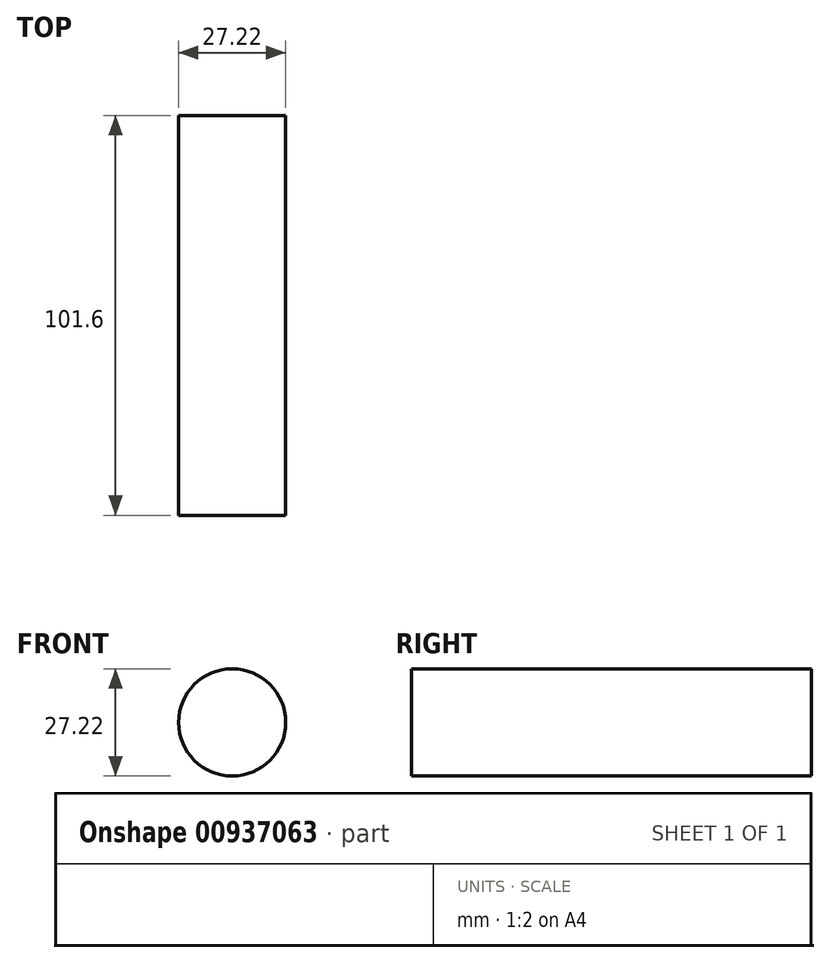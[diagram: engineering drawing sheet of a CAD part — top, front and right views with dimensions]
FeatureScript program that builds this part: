
annotation { "Feature Type Name" : "Feature", "Feature Type Description" : "" }
export const myFeature = defineFeature(function(context is Context, id is Id, definition is map)
    precondition{}
    {
        {
            var Q0;
            Q0=qCreatedBy(makeId("Front.planeOp"),FACE);
            var sketch = newSketch(context, id + "F0", { "sketchPlane" : qUnion([Q0])});
            skCircle(sketch, "E0", {"center": v(0, 0) * mm, "radius": 13.6 * mm});
            skSolve(sketch);
        }
        {
            var Q0;
            Q0=makeQuery(id+"F0.imprint","IMPRINT",FACE,{"disambiguationData":[TD([[makeQuery(id+"F0.imprint","IMPRINT",EDGE,{"derivedFrom":sQuery(id+"F0.wireOp",EDGE,"E0")}),1.0]])]});
            extrude(context, id + "F1", {"entities" : qUnion([Q0]), "depth" : 101.6 * mm, "offsetDistance" : 25.4 * mm});
        }
    });
